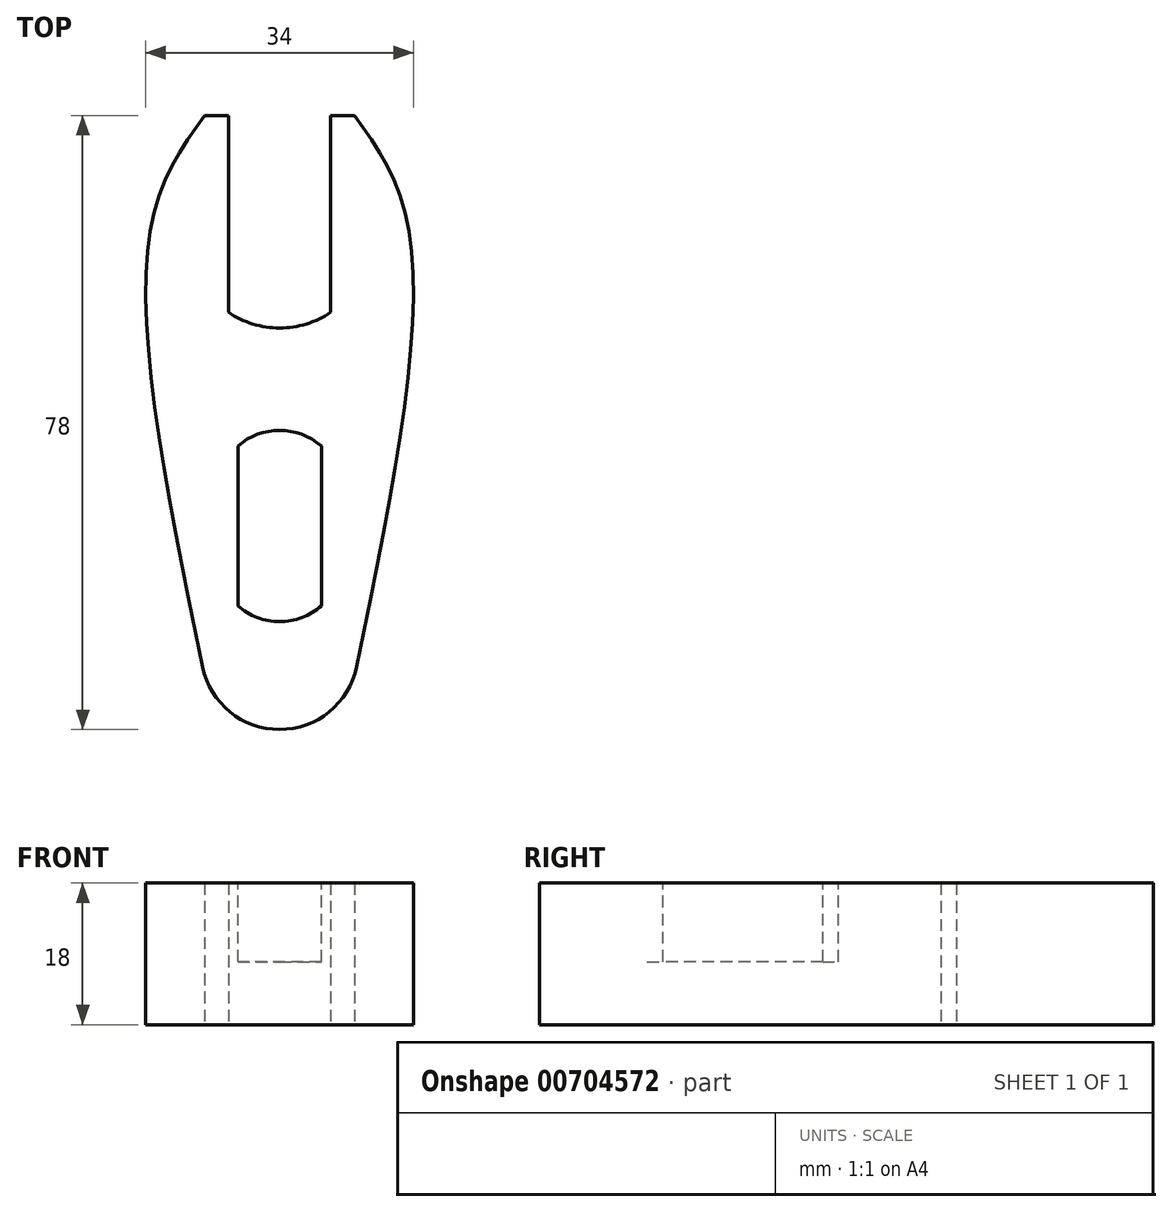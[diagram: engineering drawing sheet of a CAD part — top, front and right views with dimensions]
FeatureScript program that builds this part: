
annotation { "Feature Type Name" : "Feature", "Feature Type Description" : "" }
export const myFeature = defineFeature(function(context is Context, id is Id, definition is map)
    precondition{}
    {
        {
            var Q0;
            Q0=qCreatedBy(makeId("Top.planeOp"),FACE);
            var sketch = newSketch(context, id + "F0", { "sketchPlane" : qUnion([Q0])});
            skLineSegment(sketch, "E0.bottom", {"start": v(9.5, 39) * mm, "end": v(6.5, 39) * mm});
            skPoint(sketch, "E0.middle", {"position": v(0, 0) * mm});
            skLineSegment(sketch, "E1", {"start": v(0, 39) * mm, "end": v(0, -46.85) * mm, "construction": true});
            skPoint(sketch, "E2", {"position": v(-9.5, 39) * mm});
            skPoint(sketch, "E3.MirrorP", {"position": v(9.5, 39) * mm});
            skPoint(sketch, "E4", {"position": v(-16.5, 24) * mm});
            skArc(sketch, "E5", {"start": v(-9.8, -31.03) * mm, "mid": v(0, -39) * mm, "end": v(9.8, -31.03) * mm});
            skFitSpline(sketch, "E6", {"points": [v(-9.5, 39) * mm, v(-16.5, 24) * mm, v(-9.8, -31.03) * mm], "startDerivative": vector(-25.15, -34.92) * mm, "endDerivative": vector(20.51, -98.91) * mm});
            skFitSpline(sketch, "E7.MirrorCS", {"points": [v(9.5, 39) * mm, v(16.5, 24) * mm, v(9.8, -31.03) * mm], "startDerivative": vector(25.15, -34.92) * mm, "endDerivative": vector(-20.51, -98.91) * mm});
            skLineSegment(sketch, "E8.trimOffspring", {"start": v(-6.5, 39) * mm, "end": v(-9.5, 39) * mm});
            skLineSegment(sketch, "E9.0", {"start": v(-6.5, 39) * mm, "end": v(-6.5, 14) * mm});
            skLineSegment(sketch, "E10.0", {"start": v(6.5, 39) * mm, "end": v(6.5, 14) * mm});
            skPoint(sketch, "E11.orphan", {"position": v(-7.5, 39) * mm});
            skPoint(sketch, "E12.orphan", {"position": v(7.5, 39) * mm});
            skArc(sketch, "E13", {"start": v(0, 12) * mm, "mid": v(3.4, 12.51) * mm, "end": v(6.5, 14) * mm});
            skArc(sketch, "E14.MirrorCS", {"start": v(0, 12) * mm, "mid": v(-3.4, 12.51) * mm, "end": v(-6.5, 14) * mm});
            skSolve(sketch);
        }
        {
            var Q0;
            Q0=makeQuery(id+"F0.imprint","IMPRINT",FACE,{"disambiguationData":[TD([[makeQuery(id+"F0.imprint","IMPRINT",EDGE,{"derivedFrom":sQuery(id+"F0.wireOp",EDGE,"E0.bottom")}),1.0]])]});
            extrude(context, id + "F1", {"entities" : qUnion([Q0]), "depth" : 18 * mm, "offsetDistance" : 25 * mm});
        }
        {
            var Q0;
            Q0=makeQuery(id+"F1.opExtrude","CAP_FACE",FACE,{"disambiguationData":[OSD([sQuery(id+"F0.wireOp",EDGE,"E0.bottom"),sQuery(id+"F0.wireOp",EDGE,"E5"),sQuery(id+"F0.wireOp",EDGE,"E6"),sQuery(id+"F0.wireOp",EDGE,"E7.MirrorCS"),sQuery(id+"F0.wireOp",EDGE,"E8.trimOffspring"),sQuery(id+"F0.wireOp",EDGE,"E9.0"),sQuery(id+"F0.wireOp",EDGE,"E10.0"),sQuery(id+"F0.wireOp",EDGE,"E13"),sQuery(id+"F0.wireOp",EDGE,"E14.MirrorCS")])],"isStart":false});
            var sketch = newSketch(context, id + "F2", { "sketchPlane" : qUnion([Q0])});
            skPoint(sketch, "E15", {"position": v(0, -1) * mm});
            skPoint(sketch, "E16.middle", {"position": v(0, -14) * mm});
            skPoint(sketch, "E17.second.point", {"position": v(0, -25.3) * mm});
            skPoint(sketch, "E18.orphan", {"position": v(-6, -1) * mm});
            skPoint(sketch, "E19.orphan", {"position": v(6, -1) * mm});
            skPoint(sketch, "E20.orphan", {"position": v(-6, -27) * mm});
            skPoint(sketch, "E21.orphan", {"position": v(6, -27) * mm});
            skLineSegment(sketch, "E22.0", {"start": v(-5.3, -3) * mm, "end": v(-5.3, -23.3) * mm});
            skLineSegment(sketch, "E23.0", {"start": v(5.3, -3) * mm, "end": v(5.3, -23.3) * mm});
            skArc(sketch, "E24", {"start": v(0, -25.3) * mm, "mid": v(2.83, -24.78) * mm, "end": v(5.3, -23.3) * mm});
            skArc(sketch, "E25.MirrorCS", {"start": v(0, -25.3) * mm, "mid": v(-2.83, -24.78) * mm, "end": v(-5.3, -23.3) * mm});
            skArc(sketch, "E26", {"start": v(5.3, -3) * mm, "mid": v(2.83, -1.52) * mm, "end": v(0, -1) * mm});
            skArc(sketch, "E27.MirrorCS", {"start": v(-5.3, -3) * mm, "mid": v(-2.83, -1.52) * mm, "end": v(0, -1) * mm});
            skSolve(sketch);
        }
        {
            var Q0;
            Q0 = qSketchRegion(id + "F2", true);
            extrude(context, id + "F3", {"entities" : qUnion([Q0]), "operationType" : NewBodyOperationType.REMOVE, "oppositeDirection" : true, "depth" : 10 * mm, "offsetDistance" : 25 * mm});
        }
    });
